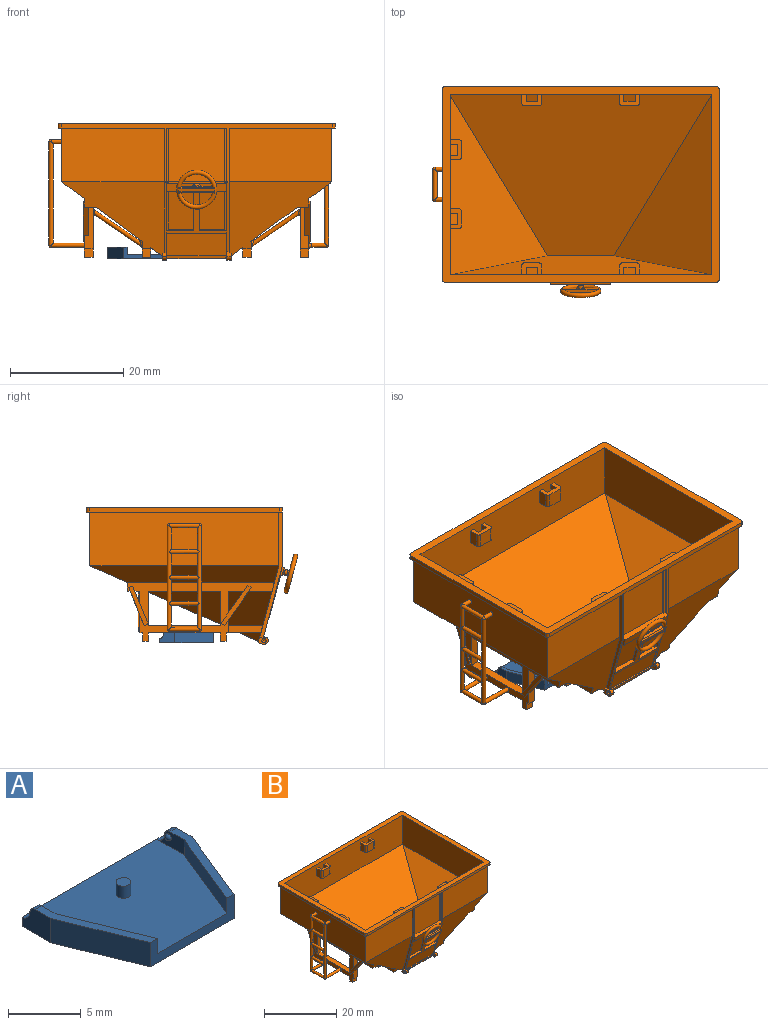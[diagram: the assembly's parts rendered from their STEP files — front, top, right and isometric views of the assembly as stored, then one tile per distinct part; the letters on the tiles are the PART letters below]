
ASSEMBLY  parts=2 mates=2
PART A: 22 faces, bbox 13.7x9.7x2 mm
  f0: plane 12.45x9.65mm, normal (0,0,1), area 99.5mm2, adj f3,f7,f8,f10,f11,f15,f20
  f1: plane 2.79x2.03mm, normal (-1,0,0), area 4.8mm2, adj f2,f6,f9,f15,f16,f19
  f2: plane 6.86x2.79mm, normal (-0.93,-0.38,0), area 15mm2, adj f1,f3,f6,f9
  f3: plane 8.13x2.03mm, normal (0,-1,0), area 7.9mm2, adj f0,f2,f4,f6,f8,f9,f10,f12
  f4: plane 6.86x2.79mm, normal (0.93,-0.38,0), area 15mm2, adj f3,f5,f6,f12
  f5: plane 2.79x2.03mm, normal (1,0,0), area 4.8mm2, adj f4,f6,f12,f15,f17,f18
  f6: plane 13.72x9.65mm, normal (0,0,-1), area 113.2mm2, adj f1,f2,f3,f4,f5,f15
  f7: plane 2.67x1.27mm, normal (1,0,0), area 2.3mm2, adj f0,f8,f9,f14,f16,f19
  f8: plane 6.98x2.84mm, normal (0.93,0.38,0), area 9.6mm2, adj f0,f3,f7,f9
  f9: plane 8.38x3.48mm, normal (0,0,1), area 5.7mm2, adj f1,f2,f3,f7,f8,f19
  f10: plane 6.98x2.84mm, normal (-0.93,0.38,0), area 9.6mm2, adj f0,f3,f11,f12
  f11: plane 2.67x1.27mm, normal (-1,0,0), area 2.3mm2, adj f0,f10,f12,f13,f17,f18
  f12: plane 8.38x3.48mm, normal (0,0,1), area 5.7mm2, adj f3,f4,f5,f10,f11,f18
  f13: sphere r=0.25mm, area 0.4mm2, adj f11
  f14: sphere r=0.25mm, area 0.4mm2, adj f7
  f15: plane 13.72x0.76mm, normal (0,1,0), area 10.5mm2, adj f0,f1,f5,f6,f16,f17
  f16: cylinder r=0.76mm len=0.76mm, axis (-1,0,0), area 0.8mm2, adj f1,f7,f15,f19
  f17: cylinder r=0.76mm len=0.76mm, axis (-1,0,0), area 0.8mm2, adj f5,f11,f15,f18
  f18: cylinder r=0.51mm len=0.64mm, axis (1,0,0), area 0.5mm2, adj f5,f11,f12,f17
  f19: cylinder r=0.51mm len=0.64mm, axis (1,0,0), area 0.5mm2, adj f1,f7,f9,f16
  f20: cylinder r=0.51mm len=1.02mm, axis (0,0,-1), area 3.2mm2, adj f0,f21
  f21: plane 1.02x1.02mm, normal (0,0,1), area 0.8mm2, adj f20
PART B: 340 faces, bbox 50.9x37.7x24.5 mm
  f0: plane 31.81x9.9mm, normal (1,0,0), area 307.3mm2, adj f1,f5,f7,f11,f12,f33,f305,f326
  f1: plane 2.54x1.52mm, normal (0,-1,0), area 3.9mm2, adj f0,f2,f337,f339
  f2: cylinder r=0.51mm len=2.54mm, axis (0,0,-1), area 2mm2, adj f1,f3,f337,f339
  f3: plane 2.54x2.54mm, normal (1,0,0), area 6.5mm2, adj f2,f4,f337,f339
  f4: cylinder r=0.51mm len=2.54mm, axis (0,0,-1), area 2mm2, adj f3,f337,f338,f339
  f5: plane 2.54x1.27mm, normal (0,1,0), area 3.2mm2, adj f0,f6,f337,f339
  f6: plane 2.54x2.03mm, normal (-1,0,0), area 5.2mm2, adj f5,f336,f337,f339
  f7: plane 46.1x28.5mm, normal (0,-0.41,0.91), area 907.7mm2, adj f0,f8,f9,f10,f11,f305
  f8: plane 31.81x9.9mm, normal (-1,0,0), area 315mm2, adj f7,f9,f12,f33,f305
  f9: plane 31.57x17.18mm, normal (-0.59,0,0.81), area 337.7mm2, adj f7,f8,f10,f12
  f10: plane 45.33x12.37mm, normal (0,0.97,0.26), area 365.5mm2, adj f7,f9,f11,f12
  f11: plane 31.57x17.18mm, normal (0.59,0,0.81), area 337.7mm2, adj f0,f7,f10,f12
  f12: plane 46.1x10.19mm, normal (0,1,0), area 461.8mm2, adj f0,f8,f9,f10,f11,f13,f17,f19
  f13: plane 2.54x1.52mm, normal (1,0,0), area 3.9mm2, adj f12,f14,f30,f32
  f14: cylinder r=0.51mm len=2.54mm, axis (0,0,-1), area 2mm2, adj f13,f15,f30,f32
  f15: plane 2.54x2.54mm, normal (0,1,0), area 6.5mm2, adj f14,f16,f30,f32
  f16: cylinder r=0.51mm len=2.54mm, axis (0,0,-1), area 2mm2, adj f15,f30,f31,f32
  f17: plane 2.54x1.27mm, normal (-1,0,0), area 3.2mm2, adj f12,f18,f30,f32
  f18: plane 2.54x2.03mm, normal (0,-1,0), area 5.2mm2, adj f17,f29,f30,f32
  f19: plane 2.54x1.52mm, normal (1,0,0), area 3.9mm2, adj f12,f20,f26,f28
  f20: cylinder r=0.51mm len=2.54mm, axis (0,0,-1), area 2mm2, adj f19,f21,f26,f28
  f21: plane 2.54x2.54mm, normal (0,1,0), area 6.5mm2, adj f20,f22,f26,f28
  f22: cylinder r=0.51mm len=2.54mm, axis (0,0,-1), area 2mm2, adj f21,f26,f27,f28
  f23: plane 2.54x1.27mm, normal (-1,0,0), area 3.2mm2, adj f12,f24,f26,f28
  f24: plane 2.54x2.03mm, normal (0,-1,0), area 5.2mm2, adj f23,f25,f26,f28
  f25: plane 2.54x1.27mm, normal (1,0,0), area 3.2mm2, adj f12,f24,f26,f28
  f26: plane 3.56x2.03mm, normal (0,0,-1), area 4.5mm2, adj f12,f19,f20,f21,f22,f23,f24,f25
  f27: plane 2.54x1.52mm, normal (-1,0,0), area 3.9mm2, adj f12,f22,f26,f28
  f28: plane 3.56x2.03mm, normal (0,0,1), area 4.5mm2, adj f12,f19,f20,f21,f22,f23,f24,f25
  f29: plane 2.54x1.27mm, normal (1,0,0), area 3.2mm2, adj f12,f18,f30,f32
  f30: plane 3.56x2.03mm, normal (0,0,-1), area 4.5mm2, adj f12,f13,f14,f15,f16,f17,f18,f29
  f31: plane 2.54x1.52mm, normal (-1,0,0), area 3.9mm2, adj f12,f16,f30,f32
  f32: plane 3.56x2.03mm, normal (0,0,1), area 4.5mm2, adj f12,f13,f14,f15,f16,f17,f18,f29
  f33: plane 48.9x34.61mm, normal (0,0,1), area 225.3mm2, adj f0,f8,f12,f34,f298,f299,f300,f301
  f34: cylinder r=0.51mm len=0.76mm, axis (0,0,-1), area 0.6mm2, adj f33,f35,f298,f304
  f35: plane 48.9x34.61mm, normal (0,0,-1), area 97mm2, adj f34,f36,f292,f293,f294,f295,f296,f297
  f36: plane 22.1x4mm, normal (-1,0,0), area 14.3mm2, adj f35,f37,f289,f290,f291,f292,f304
  f37: cylinder r=0.64mm len=0.38mm, axis (1,0,0), area 0.1mm2, adj f36,f38,f289,f304
  f38: plane 9.69x0.39mm, normal (1,0,0), area 3.7mm2, adj f37,f39,f286,f287,f288,f304
  f39: plane 10.67x0.64mm, normal (0,0,-1), area 6.6mm2, adj f38,f40,f282,f283,f284,f285,f286,f304
  f40: plane 9.69x0.39mm, normal (-1,0,0), area 3.7mm2, adj f39,f41,f42,f282,f288,f304
  f41: cylinder r=0.25mm len=0.38mm, axis (1,0,0), area 0mm2, adj f40,f282,f283,f288
  f42: cylinder r=0.64mm len=0.38mm, axis (1,0,0), area 0.1mm2, adj f40,f43,f297,f304
  f43: plane 12.09x3.24mm, normal (0,-0.97,-0.26), area 4.8mm2, adj f42,f44,f278,f279,f280,f281,f297
  f44: plane 0.52x0.25mm, normal (1,0,0), area 0.1mm2, adj f43,f45,f226,f277
  f45: plane 10.67x0.25mm, normal (0,0.26,-0.97), area 2.7mm2, adj f44,f46,f224,f225,f226,f281
  f46: plane 4.78x1.17mm, normal (1,0,0), area 1.5mm2, adj f45,f47,f220,f221,f222,f223,f225,f289
  f47: cylinder r=0.76mm len=0.96mm, axis (1,0,0), area 1.1mm2, adj f46,f48,f220,f223
  f48: plane 1.79x1.26mm, normal (-1,0,0), area 1.4mm2, adj f47,f49,f218,f220,f223,f290,f291
  f49: plane 1.02x0.53mm, normal (0,0.97,0.26), area 0.3mm2, adj f48,f50,f51,f217,f223
  f50: cylinder r=0.25mm len=0.8mm, axis (0,0.97,0.26), area 0.3mm2, adj f49,f51,f222,f223
  f51: plane 10.84x0.85mm, normal (0,0.26,-0.97), area 9.1mm2, adj f49,f50,f52,f216,f217,f222
  f52: cylinder r=0.25mm len=1.15mm, axis (0,-0.97,-0.26), area 0.4mm2, adj f51,f53,f212,f213,f214,f216
  f53: plane 0.76x0.15mm, normal (0,0.97,0.26), area 0mm2, adj f52,f54,f211,f212,f216
  f54: plane 1.97x1.26mm, normal (1,0,0), area 1.4mm2, adj f53,f55,f206,f207,f208,f209,f211,f212
  f55: plane 18.13x13.08mm, normal (0,-0.97,-0.26), area 127.6mm2, adj f54,f56,f198,f199,f200,f201,f202,f203
  f56: plane 33.34x4mm, normal (0.59,0,-0.81), area 146.2mm2, adj f55,f57,f148,f197,f198,f295
  f57: plane 47.63x6.58mm, normal (0,0.41,-0.91), area 314.5mm2, adj f56,f58,f147,f294
  f58: plane 33.34x4mm, normal (-0.59,0,-0.81), area 147.4mm2, adj f57,f59,f291,f293
  f59: plane 25.97x10.39mm, normal (-1,0,0), area 74.8mm2, adj f58,f60,f63,f64,f66,f68,f69,f70
  f60: plane 6.7x2.71mm, normal (0,-0.93,0.37), area 3.6mm2, adj f59,f61,f62,f63,f124,f126,f199
  f61: plane 4.18x1.69mm, normal (1,0,0), area 2.6mm2, adj f60,f124,f125,f199
  f62: plane 6.99x3.42mm, normal (-1,0,0), area 5.5mm2, adj f60,f63,f125,f126
  f63: plane 0.71x0.29mm, normal (0,0.37,0.93), area 0.2mm2, adj f59,f60,f62,f125
  f64: plane 0.62x0.44mm, normal (0,-0.57,0.82), area 0.2mm2, adj f59,f65,f66,f69
  f65: plane 7.14x5.32mm, normal (-1,0,0), area 6.2mm2, adj f64,f66,f68,f69
  f66: plane 6.7x4.69mm, normal (0,0.82,0.57), area 5.5mm2, adj f59,f64,f65,f67,f68,f70,f199
  f67: plane 4.98x3.49mm, normal (1,0,0), area 4mm2, adj f66,f69,f70,f199
  f68: plane 0.62x0.44mm, normal (0,0.57,-0.82), area 0.2mm2, adj f59,f65,f66,f69
  f69: plane 6.7x4.69mm, normal (0,-0.82,-0.57), area 6.7mm2, adj f59,f64,f65,f67,f68,f70,f199
  f70: plane 7.34x1.52mm, normal (0,-1,0), area 10.2mm2, adj f59,f66,f67,f69,f71,f115,f199
  f71: plane 15.75x8.86mm, normal (1,0,0), area 40.1mm2, adj f70,f72,f115,f116,f117,f118,f119,f120
  f72: bspline ~1.54x1.27mm, area 1.4mm2, adj f71,f73
  f73: cylinder r=0.38mm len=9.28mm, axis (-0.83,0,0.56), area 23.6mm2, adj f72,f74
  f74: bspline ~1.54x1.27mm, area 1.4mm2, adj f73,f75
  f75: plane 22.08x9.22mm, normal (-1,0,0), area 38.2mm2, adj f74,f76,f103,f104,f105,f106,f107,f108
  f76: plane 35.5x19.6mm, normal (0,0.41,-0.91), area 501.5mm2, adj f75,f77,f78,f79,f103,f104,f199,f200
  f77: plane 5.92x1.52mm, normal (0,-1,0), area 9mm2, adj f76,f201,f202,f204
  f78: plane 22.16x8.24mm, normal (-0.59,0,-0.81), area 149.1mm2, adj f76,f104,f199,f291
  f79: plane 21.45x8.86mm, normal (1,0,0), area 33.1mm2, adj f76,f80,f99,f100,f101,f102,f103,f104
  f80: plane 7.82x2.65mm, normal (-0.32,0,0.95), area 5.8mm2, adj f79,f81,f82,f101,f102,f114
  f81: plane 0.72x0.25mm, normal (-0.95,0,-0.32), area 0.2mm2, adj f80,f82,f99,f114
  f82: plane 18.02x6.75mm, normal (0,1,0), area 27.6mm2, adj f80,f81,f83,f84,f94,f95,f96,f97
  f83: plane 0.72x0.25mm, normal (-0.95,0,0.32), area 0.2mm2, adj f82,f100,f102,f114
  f84: plane 8.76x2.97mm, normal (-0.32,0,-0.95), area 6.7mm2, adj f82,f85,f94,f99,f101,f204
  f85: plane 7.34x1.52mm, normal (0,1,0), area 10mm2, adj f84,f86,f94,f95,f96,f97,f98,f199
  f86: plane 1.52x0.51mm, normal (0,0,-1), area 0.8mm2, adj f85,f87,f202,f204
  f87: plane 1.52x1.52mm, normal (0,1,0), area 2.3mm2, adj f86,f88,f202,f204
  f88: plane 1.52x1.02mm, normal (0,0,-1), area 1.5mm2, adj f87,f89,f202,f204
  f89: plane 1.52x1.52mm, normal (0,-1,0), area 2.3mm2, adj f88,f90,f202,f204
  f90: plane 12.7x1.52mm, normal (0,0,-1), area 19.4mm2, adj f89,f91,f202,f204
  f91: plane 1.52x1.52mm, normal (0,1,0), area 2.3mm2, adj f90,f92,f202,f204
  f92: plane 1.52x1.02mm, normal (0,0,-1), area 1.5mm2, adj f91,f93,f202,f204
  f93: plane 1.52x1.52mm, normal (0,-1,0), area 2.3mm2, adj f92,f202,f203,f204
  f94: plane 0.72x0.25mm, normal (0.95,0,-0.32), area 0.2mm2, adj f82,f84,f85,f95
  f95: plane 7.82x2.65mm, normal (0.32,0,0.95), area 5.8mm2, adj f82,f85,f94,f96,f101,f204
  f96: plane 7.82x2.65mm, normal (0.32,0,-0.95), area 5.8mm2, adj f82,f85,f95,f97,f101,f204
  f97: plane 0.72x0.25mm, normal (0.95,0,0.32), area 0.2mm2, adj f82,f85,f96,f98
  f98: plane 8.76x2.97mm, normal (-0.32,0,0.95), area 6.7mm2, adj f82,f85,f97,f100,f101,f204
  f99: plane 8.76x2.97mm, normal (0.32,0,-0.95), area 6.7mm2, adj f79,f81,f82,f84,f101,f114
  f100: plane 8.76x2.97mm, normal (0.32,0,0.95), area 6.7mm2, adj f79,f82,f83,f98,f101,f114
  f101: plane 16.26x6.32mm, normal (0,-1,0), area 25.2mm2, adj f79,f80,f84,f95,f96,f98,f99,f100
  f102: plane 7.82x2.65mm, normal (-0.32,0,-0.95), area 5.8mm2, adj f79,f80,f82,f83,f101,f114
  f103: plane 5.92x1.52mm, normal (0,-1,0), area 9mm2, adj f75,f76,f79,f104
  f104: plane 20.19x1.52mm, normal (0,0,1), area 21.1mm2, adj f75,f76,f78,f79,f103,f291
  f105: plane 6.14x1.52mm, normal (0,0,-1), area 9.4mm2, adj f75,f79,f106,f291
  f106: plane 1.52x1.52mm, normal (0,-1,0), area 2.3mm2, adj f75,f79,f105,f107
  f107: plane 1.52x1.02mm, normal (0,0,-1), area 1.5mm2, adj f75,f79,f106,f108
  f108: plane 1.52x1.52mm, normal (0,1,0), area 2.3mm2, adj f75,f79,f107,f109
  f109: plane 12.7x1.52mm, normal (0,0,-1), area 19.4mm2, adj f75,f79,f108,f110
  f110: plane 1.52x1.52mm, normal (0,-1,0), area 2.3mm2, adj f75,f79,f109,f111
  f111: plane 1.52x1.02mm, normal (0,0,-1), area 1.5mm2, adj f75,f79,f110,f112
  f112: plane 1.52x1.52mm, normal (0,1,0), area 2.3mm2, adj f75,f79,f111,f113
  f113: plane 1.52x0.51mm, normal (0,0,-1), area 0.8mm2, adj f75,f79,f112,f114
  f114: plane 7.34x1.52mm, normal (0,1,0), area 10mm2, adj f75,f79,f80,f81,f83,f99,f100,f102
  f115: plane 1.52x0.51mm, normal (0,0,-1), area 0.8mm2, adj f59,f70,f71,f116
  f116: plane 1.52x1.52mm, normal (0,-1,0), area 2.3mm2, adj f59,f71,f115,f117
  f117: plane 1.52x1.02mm, normal (0,0,-1), area 1.5mm2, adj f59,f71,f116,f118
  f118: plane 1.52x1.52mm, normal (0,1,0), area 2.3mm2, adj f59,f71,f117,f119
  f119: plane 12.7x1.52mm, normal (0,0,-1), area 19.4mm2, adj f59,f71,f118,f120
  f120: plane 1.52x1.52mm, normal (0,-1,0), area 2.3mm2, adj f59,f71,f119,f121
  f121: plane 1.52x1.02mm, normal (0,0,-1), area 1.5mm2, adj f59,f71,f120,f122
  f122: plane 1.52x1.52mm, normal (0,1,0), area 2.3mm2, adj f59,f71,f121,f123
  f123: plane 1.52x0.51mm, normal (0,0,-1), area 0.8mm2, adj f59,f71,f122,f124
  f124: plane 7.34x1.52mm, normal (0,1,0), area 9.6mm2, adj f59,f60,f61,f71,f123,f125,f199
  f125: plane 6.7x2.71mm, normal (0,0.93,-0.37), area 5.3mm2, adj f59,f61,f62,f63,f124,f126,f199
  f126: plane 0.71x0.29mm, normal (0,-0.37,-0.93), area 0.2mm2, adj f59,f60,f62,f125
  f127: plane 6.07x1.52mm, normal (0,1,0), area 9.2mm2, adj f59,f71,f129,f199
  f128: plane 6.07x1.52mm, normal (0,-1,0), area 9.2mm2, adj f59,f71,f129,f199
  f129: plane 12.7x1.52mm, normal (0,0,1), area 19.4mm2, adj f59,f71,f127,f128
  f130: cylinder r=0.38mm len=5.91mm, axis (-1,0,0), area 13.6mm2, adj f59,f131,f142,f143,f144,f145
  f131: cylinder r=0.38mm len=5.33mm, axis (0,1,0), area 8.9mm2, adj f130,f132,f133,f142,f143,f144,f145,f146
  f132: sphere r=0.38mm, area 0.2mm2, adj f131,f133,f146
  f133: cylinder r=0.38mm len=18.29mm, axis (0,0,1), area 41.1mm2, adj f131,f132,f134,f137,f138,f139,f140,f141
  f134: cylinder r=0.38mm len=5.33mm, axis (0,-1,0), area 12.3mm2, adj f133,f135,f136,f140,f141,f145
  f135: cylinder r=0.38mm len=1.91mm, axis (1,0,0), area 4.3mm2, adj f134,f136,f145,f293
  f136: sphere r=0.38mm, area 0.2mm2, adj f134,f135,f145
  f137: cylinder r=0.38mm len=5.33mm, axis (0,-1,0), area 11.6mm2, adj f133,f145
  f138: cylinder r=0.38mm len=5.33mm, axis (0,-1,0), area 11.6mm2, adj f133,f145
  f139: cylinder r=0.38mm len=5.33mm, axis (0,-1,0), area 11.6mm2, adj f133,f145
  f140: cylinder r=0.38mm len=1.91mm, axis (1,0,0), area 4.3mm2, adj f133,f134,f141,f293
  f141: sphere r=0.38mm, area 0.2mm2, adj f133,f134,f140
  f142: plane 5.33x0.38mm, normal (1,0,0), area 1.8mm2, adj f130,f131,f143,f146
  f143: plane 5.33x0.38mm, normal (0,0,-1), area 2mm2, adj f130,f131,f142,f146
  f144: sphere r=0.38mm, area 0.2mm2, adj f130,f131,f145
  f145: cylinder r=0.38mm len=18.29mm, axis (0,0,1), area 41.1mm2, adj f130,f131,f134,f135,f136,f137,f138,f139
  f146: cylinder r=0.38mm len=5.91mm, axis (1,0,0), area 13.6mm2, adj f59,f131,f132,f133,f142,f143
  f147: plane 39.62x1.52mm, normal (0,1,0), area 60.4mm2, adj f57,f59,f198,f199
  f148: cylinder r=0.38mm len=10.81mm, axis (0,0,-1), area 23.5mm2, adj f56,f149,f150,f151,f195,f196
  f149: cylinder r=0.38mm len=5.33mm, axis (0,1,0), area 12.8mm2, adj f148,f197
  f150: cylinder r=0.38mm len=5.33mm, axis (0,1,0), area 12.8mm2, adj f148,f197
  f151: cylinder r=0.38mm len=5.33mm, axis (0,-1,0), area 8.9mm2, adj f148,f152,f153,f193,f194,f195,f196,f197
  f152: plane 5.33x0.38mm, normal (-1,0,0), area 1.8mm2, adj f151,f153,f194,f196
  f153: cylinder r=0.38mm len=2.73mm, axis (-1,0,0), area 6mm2, adj f151,f152,f154,f190,f191,f192,f193,f194
  f154: torus R=0.76mm, axis (1,0,0), area 0.6mm2, adj f153,f155,f190,f192
  f155: plane 4.49x1.27mm, normal (1,0,0), area 5.1mm2, adj f154,f156,f188,f189
  f156: plane 12.72x1.54mm, normal (0,0,-1), area 19.4mm2, adj f155,f157,f160,f171,f187,f192,f198
  f157: bspline ~0.95x0.42mm, area 0.3mm2, adj f156,f158,f188,f196
  f158: torus R=0.76mm, axis (1,0,0), area 0.6mm2, adj f157,f159,f196,f198
  f159: bspline ~0.95x0.42mm, area 0.3mm2, adj f158,f188,f189,f196
  f160: plane 1.52x1.52mm, normal (0,-1,0), area 2.3mm2, adj f156,f161,f171,f198
  f161: plane 1.52x1.02mm, normal (0,0,-1), area 1.5mm2, adj f160,f162,f171,f198
  f162: plane 1.52x1.52mm, normal (0,1,0), area 2.3mm2, adj f161,f163,f171,f198
  f163: plane 1.52x0.51mm, normal (0,0,-1), area 0.8mm2, adj f162,f164,f171,f198
  f164: plane 7.34x1.52mm, normal (0,1,0), area 9.6mm2, adj f163,f165,f169,f170,f171,f198,f199
  f165: plane 6.7x2.71mm, normal (0,-0.93,0.37), area 3.6mm2, adj f164,f166,f167,f168,f170,f198,f199
  f166: plane 0.71x0.29mm, normal (0,0.37,0.93), area 0.2mm2, adj f165,f167,f169,f198
  f167: plane 6.99x3.42mm, normal (1,0,0), area 5.5mm2, adj f165,f166,f168,f169
  f168: plane 0.71x0.29mm, normal (0,-0.37,-0.93), area 0.2mm2, adj f165,f167,f169,f198
  f169: plane 6.7x2.71mm, normal (0,0.93,-0.37), area 5.3mm2, adj f164,f166,f167,f168,f170,f198,f199
  f170: plane 4.18x1.69mm, normal (-1,0,0), area 2.6mm2, adj f164,f165,f169,f199
  f171: plane 15.75x8.86mm, normal (-1,0,0), area 40.1mm2, adj f156,f160,f161,f162,f163,f164,f172,f175
  f172: bspline ~1.54x1.27mm, area 1.3mm2, adj f171,f173
  f173: cylinder r=0.38mm len=9.28mm, axis (-0.83,0,-0.56), area 23.6mm2, adj f172,f174
  f174: bspline ~1.54x1.27mm, area 1.4mm2, adj f173,f202
  f175: plane 6.07x1.52mm, normal (0,-1,0), area 9.2mm2, adj f171,f189,f198,f199
  f176: plane 6.07x1.52mm, normal (0,1,0), area 9.2mm2, adj f171,f189,f198,f199
  f177: plane 7.34x1.52mm, normal (0,-1,0), area 10.2mm2, adj f171,f178,f182,f183,f184,f198,f199
  f178: plane 6.7x4.69mm, normal (0,-0.82,-0.57), area 6.7mm2, adj f177,f179,f180,f181,f183,f198,f199
  f179: plane 0.62x0.44mm, normal (0,-0.57,0.82), area 0.2mm2, adj f178,f180,f182,f198
  f180: plane 7.14x5.32mm, normal (1,0,0), area 6.2mm2, adj f178,f179,f181,f182
  f181: plane 0.62x0.44mm, normal (0,0.57,-0.82), area 0.2mm2, adj f178,f180,f182,f198
  f182: plane 6.7x4.69mm, normal (0,0.82,0.57), area 5.5mm2, adj f177,f179,f180,f181,f183,f198,f199
  f183: plane 4.98x3.49mm, normal (-1,0,0), area 4mm2, adj f177,f178,f182,f199
  f184: plane 1.52x0.51mm, normal (0,0,-1), area 0.8mm2, adj f171,f177,f185,f198
  f185: plane 1.52x1.52mm, normal (0,-1,0), area 2.3mm2, adj f171,f184,f186,f198
  f186: plane 1.52x1.02mm, normal (0,0,-1), area 1.5mm2, adj f171,f185,f187,f198
  f187: plane 1.52x1.52mm, normal (0,1,0), area 2.3mm2, adj f156,f171,f186,f198
  f188: torus R=0.76mm, axis (1,0,0), area 0.6mm2, adj f155,f157,f159,f196
  f189: plane 12.72x1.54mm, normal (0,0,1), area 19.4mm2, adj f155,f159,f171,f175,f176,f190,f198
  f190: bspline ~0.95x0.42mm, area 0.3mm2, adj f153,f154,f189,f191
  f191: torus R=0.76mm, axis (1,0,0), area 0.6mm2, adj f153,f190,f192,f198
  f192: bspline ~0.95x0.42mm, area 0.3mm2, adj f153,f154,f156,f191
  f193: sphere r=0.38mm, area 0.1mm2, adj f151,f153,f197
  f194: plane 5.33x0.38mm, normal (0,0,-1), area 2mm2, adj f151,f152,f153,f196
  f195: sphere r=0.38mm, area 0.2mm2, adj f148,f151,f196
  f196: cylinder r=0.38mm len=2.73mm, axis (-1,0,0), area 6mm2, adj f148,f151,f152,f157,f158,f159,f188,f194
  f197: cylinder r=0.38mm len=10.81mm, axis (0,0,-1), area 23.5mm2, adj f56,f149,f150,f151,f153,f193
  f198: plane 25.97x10.39mm, normal (1,0,0), area 67.3mm2, adj f55,f56,f147,f156,f158,f160,f161,f162
  f199: plane 39.62x25.56mm, normal (0,0,-1), area 210.9mm2, adj f55,f59,f60,f61,f66,f67,f69,f70
  f200: plane 22.16x8.24mm, normal (0.59,0,-0.81), area 149.1mm2, adj f55,f76,f199,f201
  f201: plane 20.19x1.52mm, normal (0,0,1), area 21.1mm2, adj f55,f76,f77,f200,f202,f204
  f202: plane 21.72x8.86mm, normal (1,0,0), area 38.2mm2, adj f55,f76,f77,f85,f86,f87,f88,f89
  f203: plane 6.14x1.52mm, normal (0,0,-1), area 9.4mm2, adj f55,f93,f202,f204
  f204: plane 21.45x8.86mm, normal (-1,0,0), area 33.1mm2, adj f55,f76,f77,f84,f85,f86,f87,f88
  f205: cylinder r=0.25mm len=0.99mm, axis (0,1,0), area 0.3mm2, adj f55,f208,f280,f297
  f206: plane 4.45x2.24mm, normal (0.59,0,-0.81), area 6.5mm2, adj f54,f55,f76,f204,f211
  f207: cylinder r=0.51mm len=0.76mm, axis (-1,0,0), area 0.6mm2, adj f54,f208,f213,f281
  f208: plane 1.02x0.76mm, normal (0,0,1), area 0.1mm2, adj f54,f55,f205,f207,f280,f281
  f209: cylinder r=0.38mm len=0.76mm, axis (1,0,0), area 0.3mm2, adj f54,f210
  f210: sphere r=0.38mm, area 0.9mm2, adj f209
  f211: cylinder r=0.25mm len=0.49mm, axis (0.8,-0.16,0.59), area 0.1mm2, adj f53,f54,f76,f206,f216
  f212: plane 0.83x0.76mm, normal (0,0.26,-0.97), area 0.7mm2, adj f52,f53,f54,f213
  f213: cylinder r=0.76mm len=0.96mm, axis (-1,0,0), area 1.1mm2, adj f52,f54,f207,f212,f214,f281
  f214: cylinder r=0.25mm len=1.03mm, axis (0,-0.26,0.97), area 0.3mm2, adj f52,f213,f215,f222,f281
  f215: cylinder r=0.25mm len=0.56mm, axis (0,0.97,0.26), area 0.2mm2, adj f214,f221,f225,f281
  f216: cylinder r=0.25mm len=11.78mm, axis (-1,0,0), area 1.3mm2, adj f51,f52,f53,f76,f211,f217
  f217: plane 4.46x2.42mm, normal (-0.59,0,-0.81), area 6.7mm2, adj f49,f51,f76,f79,f216,f291
  f218: cylinder r=0.38mm len=0.76mm, axis (-1,0,0), area 0.3mm2, adj f48,f219
  f219: sphere r=0.38mm, area 0.9mm2, adj f218
  f220: cylinder r=0.51mm len=0.76mm, axis (1,0,0), area 0.6mm2, adj f46,f47,f48,f290
  f221: plane 10.41x0.25mm, normal (0,-0.26,0.97), area 2.6mm2, adj f46,f215,f222,f225
  f222: plane 10.41x0.74mm, normal (0,-0.97,-0.26), area 5.3mm2, adj f46,f50,f51,f214,f221
  f223: plane 0.83x0.76mm, normal (0,0.26,-0.97), area 0.7mm2, adj f46,f47,f48,f49,f50
  f224: plane 0.52x0.25mm, normal (-1,0,0), area 0.1mm2, adj f45,f226,f277,f289
  f225: plane 10.67x3.93mm, normal (0,-0.97,-0.26), area 43.3mm2, adj f45,f46,f215,f221,f281
  f226: plane 10.67x7.45mm, normal (0,-0.97,-0.26), area 12.7mm2, adj f44,f45,f224,f227,f229,f276,f277
  f227: plane 7.09x2.35mm, normal (-1,0,0), area 3.7mm2, adj f226,f228,f229,f277
  f228: plane 6.96x1.86mm, normal (0,0.97,0.26), area 7.3mm2, adj f227,f229,f276,f277
  f229: plane 10.67x0.98mm, normal (0,0.26,-0.97), area 10.1mm2, adj f226,f227,f228,f230,f231,f232,f270,f271
  f230: plane 7.05x2.23mm, normal (1,0,0), area 2.7mm2, adj f229,f275,f277,f289
  f231: plane 1.57x0.76mm, normal (-1,0,0), area 0.6mm2, adj f229,f232,f288,f289
  f232: plane 5.33x1.47mm, normal (0,-0.97,-0.26), area 7.2mm2, adj f229,f231,f233,f288
  f233: torus R=0.76mm, axis (0,-0.97,-0.26), area 1.5mm2, adj f232,f234,f270
  f234: cylinder r=0.51mm len=1.18mm, axis (0,0.97,0.26), area 1.8mm2, adj f233,f235,f265,f266,f267,f268,f269
  f235: bspline ~0.59x0.26mm, area 0.1mm2, adj f234,f236,f265
  f236: plane 6.3x0.52mm, normal (0,0.26,-0.97), area 2.9mm2, adj f235,f237,f257,f262,f263,f264,f269
  f237: plane 2.61x0.98mm, normal (0,0.97,0.26), area 2.5mm2, adj f236,f238,f239,f240,f241,f242,f265
  f238: plane 0.04x0mm, normal (0,0.26,-0.97), area 0mm2, adj f237,f239,f264
  f239: plane 0.51x0.15mm, normal (1,0,0), area 0mm2, adj f237,f238,f264
  f240: plane 0.51x0.15mm, normal (1,0,0), area 0mm2, adj f237,f241,f264
  f241: plane 0.04x0mm, normal (0,-0.26,0.97), area 0mm2, adj f237,f240,f264
  f242: plane 6.3x0.52mm, normal (0,-0.26,0.97), area 2.9mm2, adj f237,f243,f257,f262,f264,f266,f267
  f243: cylinder r=0.25mm len=5.54mm, axis (1,0,0), area 2.2mm2, adj f242,f244,f255,f256
  f244: plane 6.62x1.25mm, normal (0,-0.97,-0.26), area 3.4mm2, adj f243,f245,f246,f247,f248,f249,f250,f251
  f245: plane 0.52x0.16mm, normal (-1,0,0), area 0mm2, adj f244,f246,f262
  f246: bspline ~0.17x0.09mm, area 0mm2, adj f244,f245,f262
  f247: bspline ~0.17x0.09mm, area 0mm2, adj f244,f248,f264
  f248: plane 0.52x0.16mm, normal (1,0,0), area 0mm2, adj f244,f247,f264
  f249: plane 0.52x0.16mm, normal (1,0,0), area 0mm2, adj f244,f250,f264
  f250: bspline ~0.17x0.08mm, area 0mm2, adj f244,f249,f264
  f251: bspline ~0.39x0.32mm, area 0mm2, adj f244,f263,f264
  f252: bspline ~0.4x0.32mm, area 0mm2, adj f244,f262,f263
  f253: bspline ~0.17x0.08mm, area 0mm2, adj f244,f254,f262
  f254: plane 0.52x0.16mm, normal (-1,0,0), area 0mm2, adj f244,f253,f262
  f255: bspline ~0.36x0.31mm, area 0mm2, adj f243,f244,f262
  f256: bspline ~0.39x0.31mm, area 0mm2, adj f243,f244,f264
  f257: plane 2.61x0.98mm, normal (0,0.97,0.26), area 2.5mm2, adj f236,f242,f258,f259,f260,f261,f268
  f258: plane 0.04x0mm, normal (0,-0.26,0.97), area 0mm2, adj f257,f259,f262
  f259: plane 0.51x0.15mm, normal (-1,0,0), area 0mm2, adj f257,f258,f262
  f260: plane 0.51x0.15mm, normal (-1,0,0), area 0mm2, adj f257,f261,f262
  f261: plane 0.04x0mm, normal (0,0.26,-0.97), area 0mm2, adj f257,f260,f262
  f262: torus R=3.17mm, axis (0,-0.97,-0.26), area 46.5mm2, adj f236,f242,f245,f246,f252,f253,f254,f255
  f263: cylinder r=0.25mm len=5.54mm, axis (-1,0,0), area 2.2mm2, adj f236,f244,f251,f252
  f264: torus R=3.17mm, axis (0,-0.97,-0.26), area 1.3mm2, adj f236,f238,f239,f240,f241,f242,f247,f248
  f265: torus R=0.76mm, axis (0,-0.97,-0.26), area 0.3mm2, adj f234,f235,f237,f266
  f266: bspline ~0.59x0.29mm, area 0.1mm2, adj f234,f242,f265
  f267: bspline ~0.59x0.29mm, area 0.1mm2, adj f234,f242,f268
  f268: torus R=0.76mm, axis (0,-0.97,-0.26), area 0.3mm2, adj f234,f257,f267,f269
  f269: bspline ~0.59x0.26mm, area 0.1mm2, adj f234,f236,f268
  f270: plane 5.33x1.47mm, normal (0,-0.97,-0.26), area 7.2mm2, adj f229,f233,f279,f288
  f271: plane 6.96x1.86mm, normal (0,-0.97,-0.26), area 2.7mm2, adj f229,f272,f277,f278
  f272: plane 7.02x2.11mm, normal (-1,0,0), area 1.8mm2, adj f229,f271,f273,f277
  f273: plane 9.91x6.96mm, normal (0,-0.97,-0.26), area 71.3mm2, adj f229,f272,f274,f277
  f274: plane 7.02x2.11mm, normal (1,0,0), area 1.8mm2, adj f229,f273,f275,f277
  f275: plane 6.96x1.86mm, normal (0,-0.97,-0.26), area 2.7mm2, adj f229,f230,f274,f277
  f276: plane 7.09x2.35mm, normal (1,0,0), area 3.7mm2, adj f226,f228,f229,f277
  f277: plane 10.67x0.74mm, normal (0,-0.26,0.97), area 7.4mm2, adj f44,f224,f226,f227,f228,f230,f271,f272
  f278: plane 7.05x2.23mm, normal (-1,0,0), area 2.7mm2, adj f43,f229,f271,f277
  f279: plane 1.57x0.76mm, normal (1,0,0), area 0.6mm2, adj f43,f229,f270,f288
  f280: cylinder r=0.25mm len=0.64mm, axis (1,0,0), area 0.2mm2, adj f43,f205,f208,f281,f297
  f281: plane 4.78x1.11mm, normal (-1,0,0), area 1.2mm2, adj f43,f45,f207,f208,f213,f214,f215,f225
  f282: plane 9.53x0.38mm, normal (0,-1,0), area 3.6mm2, adj f39,f40,f41,f283
  f283: plane 9.59x0.25mm, normal (-1,0,0), area 2.4mm2, adj f39,f41,f282,f284,f288
  f284: plane 9.91x9.53mm, normal (0,-1,0), area 94.4mm2, adj f39,f283,f285,f288
  f285: plane 9.59x0.25mm, normal (1,0,0), area 2.4mm2, adj f39,f284,f286,f287,f288
  f286: plane 9.53x0.38mm, normal (0,-1,0), area 3.6mm2, adj f38,f39,f285,f287
  f287: cylinder r=0.25mm len=0.38mm, axis (1,0,0), area 0mm2, adj f38,f285,f286,f288
  f288: plane 10.67x0.98mm, normal (0,-0.26,0.97), area 10.6mm2, adj f38,f40,f41,f231,f232,f270,f279,f283
  f289: plane 12.41x3.33mm, normal (0,-0.97,-0.26), area 4.9mm2, adj f36,f37,f46,f224,f230,f231,f290
  f290: plane 1.02x0.76mm, normal (0,0,1), area 0.5mm2, adj f36,f46,f48,f220,f289,f291
  f291: plane 18.1x13.05mm, normal (0,-0.97,-0.26), area 127.6mm2, adj f36,f48,f58,f59,f75,f78,f79,f104
  f292: plane 18.1x9.53mm, normal (0,-1,0), area 172.4mm2, adj f35,f36,f291,f293
  f293: plane 33.34x9.53mm, normal (-1,0,0), area 316.6mm2, adj f35,f58,f135,f140,f292,f294
  f294: plane 47.63x9.53mm, normal (0,1,0), area 453.6mm2, adj f35,f57,f293,f295
  f295: plane 33.34x9.53mm, normal (1,0,0), area 317.5mm2, adj f35,f56,f294,f296
  f296: plane 18.1x9.53mm, normal (0,-1,0), area 172.4mm2, adj f35,f55,f295,f297
  f297: plane 21.84x3.94mm, normal (1,0,0), area 14.1mm2, adj f35,f42,f43,f55,f205,f280,f296,f304
  f298: plane 33.59x0.76mm, normal (-1,0,0), area 25.6mm2, adj f33,f34,f35,f299
  f299: cylinder r=0.51mm len=0.76mm, axis (0,0,-1), area 0.6mm2, adj f33,f35,f298,f300
  f300: plane 47.88x0.76mm, normal (0,1,0), area 36.5mm2, adj f33,f35,f299,f301
  f301: cylinder r=0.51mm len=0.76mm, axis (0,0,1), area 0.6mm2, adj f33,f35,f300,f302
  f302: plane 33.59x0.76mm, normal (1,0,0), area 25.6mm2, adj f33,f35,f301,f303
  f303: cylinder r=0.51mm len=0.76mm, axis (0,0,1), area 0.6mm2, adj f33,f35,f302,f304
  f304: plane 47.88x10.29mm, normal (0,-1,0), area 43.7mm2, adj f33,f34,f35,f36,f37,f38,f39,f40
  f305: plane 46.1x9.79mm, normal (0,-1,0), area 443.7mm2, adj f0,f7,f8,f33,f306,f310,f312,f313
  f306: plane 2.54x1.52mm, normal (1,0,0), area 3.9mm2, adj f305,f307,f312,f314
  f307: cylinder r=0.51mm len=2.54mm, axis (0,0,-1), area 2mm2, adj f306,f308,f312,f314
  f308: plane 2.54x2.54mm, normal (0,-1,0), area 6.5mm2, adj f307,f309,f312,f314
  f309: cylinder r=0.51mm len=2.54mm, axis (0,0,-1), area 2mm2, adj f308,f312,f314,f315
  f310: plane 2.54x1.27mm, normal (-1,0,0), area 3.2mm2, adj f305,f311,f312,f314
  f311: plane 2.54x2.03mm, normal (0,1,0), area 5.2mm2, adj f310,f312,f313,f314
  f312: plane 3.56x2.03mm, normal (0,0,-1), area 4.5mm2, adj f305,f306,f307,f308,f309,f310,f311,f313
  f313: plane 2.54x1.27mm, normal (1,0,0), area 3.2mm2, adj f305,f311,f312,f314
  f314: plane 3.56x2.03mm, normal (0,0,1), area 4.5mm2, adj f305,f306,f307,f308,f309,f310,f311,f313
  f315: plane 2.54x1.52mm, normal (-1,0,0), area 3.9mm2, adj f305,f309,f312,f314
  f316: plane 2.54x1.52mm, normal (1,0,0), area 3.9mm2, adj f305,f317,f322,f324
  f317: cylinder r=0.51mm len=2.54mm, axis (0,0,-1), area 2mm2, adj f316,f318,f322,f324
  f318: plane 2.54x2.54mm, normal (0,-1,0), area 6.5mm2, adj f317,f319,f322,f324
  f319: cylinder r=0.51mm len=2.54mm, axis (0,0,-1), area 2mm2, adj f318,f322,f324,f325
  f320: plane 2.54x1.27mm, normal (-1,0,0), area 3.2mm2, adj f305,f321,f322,f324
  f321: plane 2.54x2.03mm, normal (0,1,0), area 5.2mm2, adj f320,f322,f323,f324
  f322: plane 3.56x2.03mm, normal (0,0,-1), area 4.5mm2, adj f305,f316,f317,f318,f319,f320,f321,f323
  f323: plane 2.54x1.27mm, normal (1,0,0), area 3.2mm2, adj f305,f321,f322,f324
  f324: plane 3.56x2.03mm, normal (0,0,1), area 4.5mm2, adj f305,f316,f317,f318,f319,f320,f321,f323
  f325: plane 2.54x1.52mm, normal (-1,0,0), area 3.9mm2, adj f305,f319,f322,f324
  f326: plane 2.54x1.52mm, normal (0,1,0), area 3.9mm2, adj f0,f327,f332,f334
  f327: cylinder r=0.51mm len=2.54mm, axis (0,0,-1), area 2mm2, adj f326,f328,f332,f334
  f328: plane 2.54x2.54mm, normal (1,0,0), area 6.5mm2, adj f327,f329,f332,f334
  f329: cylinder r=0.51mm len=2.54mm, axis (0,0,-1), area 2mm2, adj f328,f332,f334,f335
  f330: plane 2.54x1.27mm, normal (0,-1,0), area 3.2mm2, adj f0,f331,f332,f334
  f331: plane 2.54x2.03mm, normal (-1,0,0), area 5.2mm2, adj f330,f332,f333,f334
  f332: plane 3.56x2.03mm, normal (0,0,-1), area 4.5mm2, adj f0,f326,f327,f328,f329,f330,f331,f333
  f333: plane 2.54x1.27mm, normal (0,1,0), area 3.2mm2, adj f0,f331,f332,f334
  f334: plane 3.56x2.03mm, normal (0,0,1), area 4.5mm2, adj f0,f326,f327,f328,f329,f330,f331,f333
  f335: plane 2.54x1.52mm, normal (0,-1,0), area 3.9mm2, adj f0,f329,f332,f334
  f336: plane 2.54x1.27mm, normal (0,-1,0), area 3.2mm2, adj f0,f6,f337,f339
  f337: plane 3.56x2.03mm, normal (0,0,-1), area 4.5mm2, adj f0,f1,f2,f3,f4,f5,f6,f336
  f338: plane 2.54x1.52mm, normal (0,1,0), area 3.9mm2, adj f0,f4,f337,f339
  f339: plane 3.56x2.03mm, normal (0,0,1), area 4.5mm2, adj f0,f1,f2,f3,f4,f5,f6,f336
PLACE A t=(-17.87,6.13,-3.29)mm
PLACE B t=(-8.98,2.42,-3.04)mm fixed
MATE planar A.f20 <-> B.f109  axis (0,0,1) through (-17.87,3.91,-1.51)mm
MATE parallel A.f15 <-> B.f110  axis (0,1,0) through (-17.87,6.9,-2.91)mm
